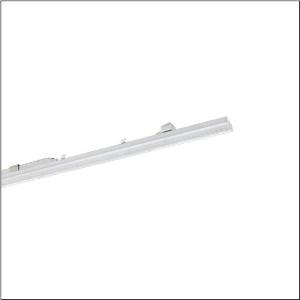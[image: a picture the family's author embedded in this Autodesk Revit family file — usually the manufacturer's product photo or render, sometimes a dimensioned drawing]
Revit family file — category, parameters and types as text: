
# Revit family: tl_l_5wd7a9h0a2b5
name_source: partatom
category: Lighting Fixtures
units: mm (PartAtom-declared; Revit-internal decimal feet)

## family parameters
Cut with Voids When Loaded = No
Host = Face
Light Source = No
Part Type = Normal
Room Calculation Point = No
Round Connector Dimension = Use Diameter
Shared = No

## types (1)
- --- (1 x LED, 860 lm, 4.5 W, 5000K)
    Apparent Load = 5 VA
    CIE Flux Codes = 49 84 98 100 100
    Color Rendering = 80
    Color Temperature = 5000K
    Default Elevation = 1800 mm
    Description = TL L, luminaire insert, of sheet steel, galvanised, coil coated, white, length: 1.500mm, width: 66mm, height: 67mm, LED rated luminous flux: 5.000lm, light colour: 850, control gear: emergency light, with terminal, 3-pole, mains connection: 230..240V, AC, 50/60Hz, rated input power: 34W, primary optical cover: cover, of PMMA, light emission: direct distribution, protection rating (complete): as luminaire, insulation class (complete): insulation class I (protective earthing), certification: CE, impact resistance: IK06, permissible ambient temperature for indoor applications: +5..+35°C, packaging unit: 1 piece
    Height = 120 mm
    Lamp = 1 x LED
    Lamp Light Flux = 860 lm
    Lamp Power = 4.5 W
    Lamp count = 1
    Length = 1690 mm
    Luminous efficacy = 191 lm/W
    Manufacturer = Siteco
    ModVariant = No
    Model = 5WD7A9H0A2B5
    Mounting Place = Ceiling
    Mounting Type = Pendant
    Number of Poles = 1
    OnlyDefault = Yes
    Power Factor = 1
    Product Name = TL L
    Product group = luminaire insert
    ProductGroupID = 901
    Protection Class = Protection class I
    Protection Degree = Degree of protection
    RLX_Detail_Level = 1
    RLX_Emergency_Light_Flux = 0 lm
    RLX_Emergency_Type = 0
    RLX_Emergency_Type_DB = No
    RlxData = <blob elided: 17373 chars, md5=487a9290>
    Socket = socket
    Standby Power = 0 W
    System Light Flux = 860 lm
    System Power = 5 W
    Type Comments = : emergency light operation: 3 h
    Type Image = l_1294382.jpg
    URL = http://relux.com
    VarID = @adj_012051
    Voltage = 0 V
    Weight = 0.00 kg
    Width = 208 mm

## geometry (parser evidence)
native form markers: Blend x4, Sweep x12
no freeform markers — native parametric forms only
